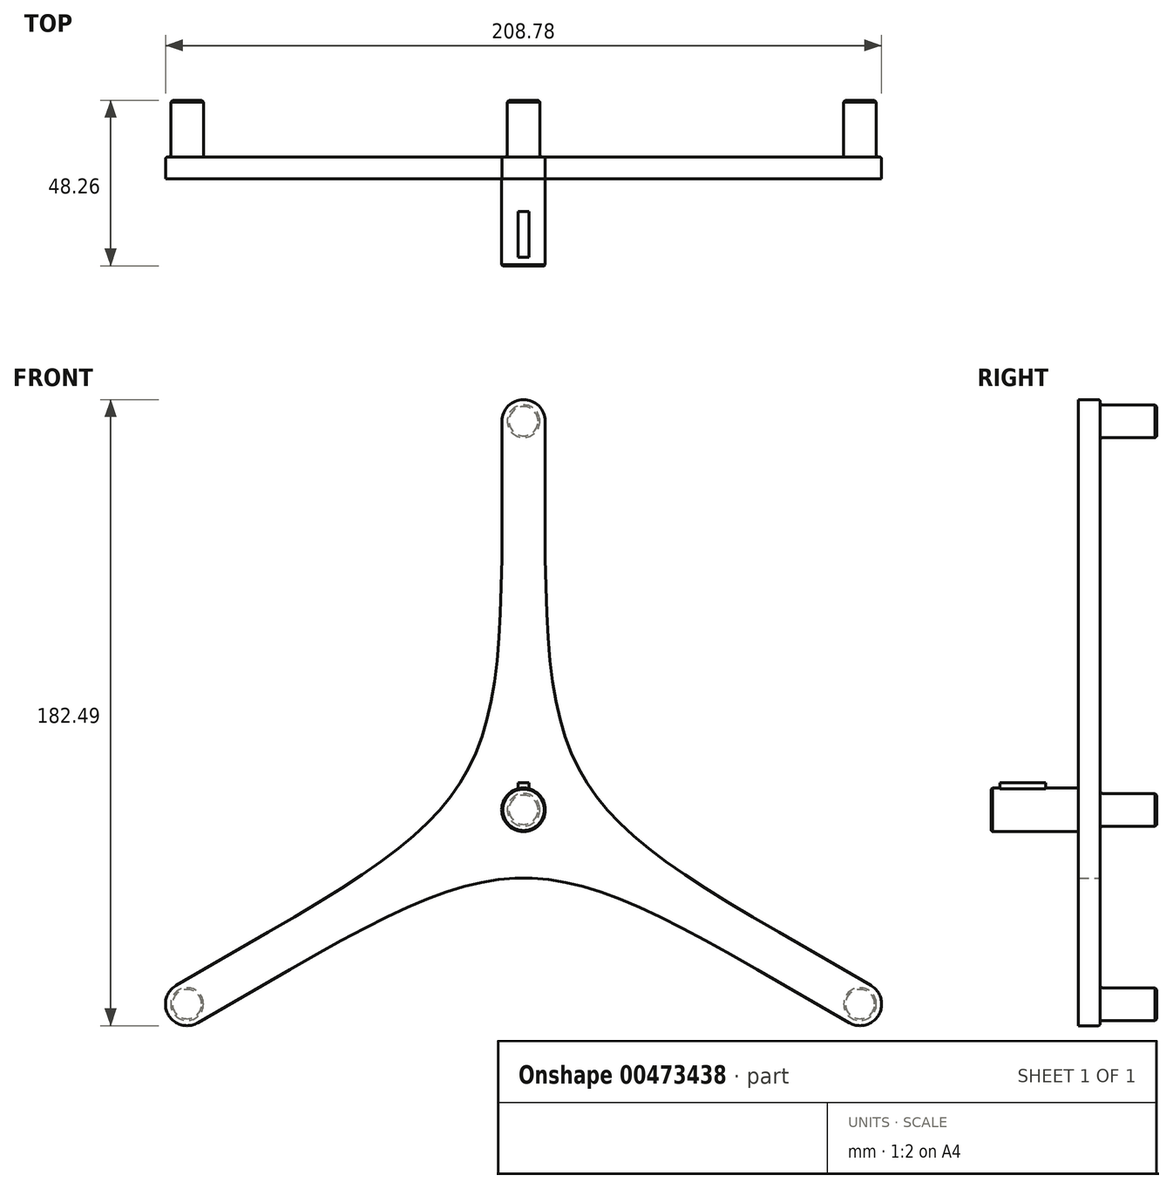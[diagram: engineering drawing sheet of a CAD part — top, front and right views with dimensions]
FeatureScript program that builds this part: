
annotation { "Feature Type Name" : "Feature", "Feature Type Description" : "" }
export const myFeature = defineFeature(function(context is Context, id is Id, definition is map)
    precondition{}
    {
        {
            var Q0;
            Q0=qCreatedBy(makeId("Front.planeOp"),FACE);
            var sketch = newSketch(context, id + "F0", { "sketchPlane" : qUnion([Q0])});
            skArc(sketch, "E0", {"start": v(-6.3, 113.26) * mm, "mid": v(0, 119.56) * mm, "end": v(6.3, 113.26) * mm});
            skArc(sketch, "E1", {"start": v(6.3, 113.26) * mm, "mid": v(0, 113.44) * mm, "end": v(-6.3, 113.26) * mm, "construction": true});
            skCircle(sketch, "E2", {"center": v(0, 113.26) * mm, "radius": 4.76 * mm});
            skLineSegment(sketch, "E3", {"start": v(-6.3, 113.26) * mm, "end": v(-6.3, 11.07) * mm});
            skArc(sketch, "E4.1.0", {"start": v(-94.94, -62.09) * mm, "mid": v(-103.54, -59.78) * mm, "end": v(-101.24, -51.18) * mm});
            skCircle(sketch, "E4.1.2", {"center": v(-98.09, -56.63) * mm, "radius": 4.76 * mm});
            skLineSegment(sketch, "E4.1.3", {"start": v(-94.94, -62.09) * mm, "end": v(-6.43, -10.99) * mm});
            skArc(sketch, "E4.1.5", {"start": v(-101.24, -51.18) * mm, "mid": v(-98.24, -56.72) * mm, "end": v(-94.94, -62.09) * mm, "construction": true});
            skArc(sketch, "E4.2.0", {"start": v(101.24, -51.18) * mm, "mid": v(103.54, -59.78) * mm, "end": v(94.94, -62.09) * mm});
            skCircle(sketch, "E4.2.2", {"center": v(98.09, -56.63) * mm, "radius": 4.76 * mm});
            skLineSegment(sketch, "E4.2.3", {"start": v(101.24, -51.18) * mm, "end": v(12.73, -0.08) * mm});
            skArc(sketch, "E4.2.5", {"start": v(94.94, -62.09) * mm, "mid": v(98.24, -56.72) * mm, "end": v(101.24, -51.18) * mm, "construction": true});
            skLineSegment(sketch, "E5", {"start": v(6.3, 11.07) * mm, "end": v(6.3, 113.26) * mm});
            skCircle(sketch, "E6", {"center": v(0, 0) * mm, "radius": 4.77 * mm});
            skLineSegment(sketch, "E7", {"start": v(6.43, -10.99) * mm, "end": v(94.94, -62.09) * mm});
            skLineSegment(sketch, "E8", {"start": v(-12.73, -0.08) * mm, "end": v(-101.24, -51.18) * mm});
            skLineSegment(sketch, "E9", {"start": v(-6.3, 11.07) * mm, "end": v(-12.73, -0.08) * mm});
            skLineSegment(sketch, "E10", {"start": v(-6.43, -10.99) * mm, "end": v(6.43, -10.99) * mm});
            skLineSegment(sketch, "E11", {"start": v(12.73, -0.08) * mm, "end": v(6.3, 11.07) * mm});
            skFitSpline(sketch, "E12", {"points": [v(6.3, 82.3) * mm, v(74.43, -35.7) * mm], "startDerivative": vector(0, -213.73) * mm, "endDerivative": vector(185.1, -106.86) * mm});
            skFitSpline(sketch, "E13", {"points": [v(-74.43, -35.7) * mm, v(-6.3, 82.3) * mm], "startDerivative": vector(185.1, 106.86) * mm, "endDerivative": vector(0, 213.73) * mm});
            skFitSpline(sketch, "E14", {"points": [v(-68.13, -46.61) * mm, v(68.13, -46.61) * mm], "startDerivative": vector(185.1, 106.86) * mm, "endDerivative": vector(185.1, -106.86) * mm});
            skSolve(sketch);
        }
        {
            var Q0;
            Q0 = qSketchRegion(id + "F0", true);
            var Q1;
            Q1=makeQuery(id+"F0.imprint","IMPRINT",FACE,{"disambiguationData":[TD([[makeQuery(id+"F0.imprint","IMPRINT",EDGE,{"derivedFrom":sQuery(id+"F0.wireOp",EDGE,"E6")}),1.0]])]});
            var Q2;
            Q2=makeQuery(id+"F0.imprint","IMPRINT",FACE,{"disambiguationData":[TD([[makeQuery(id+"F0.imprint","IMPRINT",EDGE,{"derivedFrom":sQuery(id+"F0.wireOp",EDGE,"E2")}),1.0]])]});
            var Q3;
            Q3=makeQuery(id+"F0.imprint","IMPRINT",FACE,{"disambiguationData":[TD([[makeQuery(id+"F0.imprint","IMPRINT",EDGE,{"derivedFrom":sQuery(id+"F0.wireOp",EDGE,"E4.1.2")}),1.0]])]});
            var Q4;
            Q4=makeQuery(id+"F0.imprint","IMPRINT",FACE,{"disambiguationData":[TD([[makeQuery(id+"F0.imprint","IMPRINT",EDGE,{"derivedFrom":sQuery(id+"F0.wireOp",EDGE,"E4.2.2")}),1.0]])]});
            extrude(context, id + "F1", {"entities" : qUnion([Q0, Q1, Q2, Q3, Q4]), "depth" : 6.35 * mm});
        }
        {
            var Q0;
            Q0=makeQuery(id+"F0.imprint","IMPRINT",FACE,{"disambiguationData":[TD([[makeQuery(id+"F0.imprint","IMPRINT",EDGE,{"derivedFrom":sQuery(id+"F0.wireOp",EDGE,"E4.1.2")}),1.0]])]});
            var Q1;
            Q1=makeQuery(id+"F0.imprint","IMPRINT",FACE,{"disambiguationData":[TD([[makeQuery(id+"F0.imprint","IMPRINT",EDGE,{"derivedFrom":sQuery(id+"F0.wireOp",EDGE,"E4.2.2")}),1.0]])]});
            var Q2;
            Q2=makeQuery(id+"F0.imprint","IMPRINT",FACE,{"disambiguationData":[TD([[makeQuery(id+"F0.imprint","IMPRINT",EDGE,{"derivedFrom":sQuery(id+"F0.wireOp",EDGE,"E6")}),1.0]])]});
            var Q3;
            Q3=makeQuery(id+"F0.imprint","IMPRINT",FACE,{"disambiguationData":[TD([[makeQuery(id+"F0.imprint","IMPRINT",EDGE,{"derivedFrom":sQuery(id+"F0.wireOp",EDGE,"E2")}),1.0]])]});
            extrude(context, id + "F2", {"entities" : qUnion([Q0, Q1, Q2, Q3]), "operationType" : NewBodyOperationType.ADD, "oppositeDirection" : true, "depth" : 16.5 * mm});
        }
        {
            var Q0;
            Q0=makeQuery(id+"F2.opExtrude","CAP_EDGE",EDGE,{"disambiguationData":[OSD([sQuery(id+"F0.wireOp",EDGE,"E2")])],"isStart":false});
            var Q1;
            Q1=makeQuery(id+"F2.opExtrude","CAP_EDGE",EDGE,{"disambiguationData":[OSD([sQuery(id+"F0.wireOp",EDGE,"E4.1.2")])],"isStart":false});
            var Q2;
            Q2=makeQuery(id+"F2.opExtrude","CAP_EDGE",EDGE,{"disambiguationData":[OSD([sQuery(id+"F0.wireOp",EDGE,"E4.2.2")])],"isStart":false});
            var Q3;
            Q3=makeQuery(id+"F2.opExtrude","CAP_EDGE",EDGE,{"disambiguationData":[OSD([sQuery(id+"F0.wireOp",EDGE,"E2")])],"isStart":true});
            var Q4;
            Q4=makeQuery(id+"F2.opExtrude","CAP_EDGE",EDGE,{"disambiguationData":[OSD([sQuery(id+"F0.wireOp",EDGE,"E4.1.2")])],"isStart":true});
            var Q5;
            Q5=makeQuery(id+"F2.opExtrude","CAP_EDGE",EDGE,{"disambiguationData":[OSD([sQuery(id+"F0.wireOp",EDGE,"E4.2.2")])],"isStart":true});
            var Q6;
            Q6=makeQuery(id+"F2.opExtrude","CAP_EDGE",EDGE,{"disambiguationData":[OSD([sQuery(id+"F0.wireOp",EDGE,"E6")])],"isStart":false});
            var Q7;
            Q7=makeQuery(id+"F2.opExtrude","CAP_EDGE",EDGE,{"disambiguationData":[OSD([sQuery(id+"F0.wireOp",EDGE,"E6")])],"isStart":true});
            chamfer(context, id + "F3", {"entities" : qUnion([Q0, Q1, Q2, Q3, Q4, Q5, Q6, Q7]), "width" : 0.5 * mm, "tangentPropagation" : true});
        }
        {
            var Q0;
            Q0=makeQuery(id+"F1.opExtrude","CAP_FACE",FACE,{"disambiguationData":[OSD([sQuery(id+"F0.wireOp",EDGE,"E0"),sQuery(id+"F0.wireOp",EDGE,"E3"),sQuery(id+"F0.wireOp",EDGE,"E4.1.0"),sQuery(id+"F0.wireOp",EDGE,"E4.1.3"),sQuery(id+"F0.wireOp",EDGE,"E4.2.0"),sQuery(id+"F0.wireOp",EDGE,"E4.2.3"),sQuery(id+"F0.wireOp",EDGE,"E5"),sQuery(id+"F0.wireOp",EDGE,"E7"),sQuery(id+"F0.wireOp",EDGE,"E8"),sQuery(id+"F0.wireOp",EDGE,"E12"),sQuery(id+"F0.wireOp",EDGE,"E13"),sQuery(id+"F0.wireOp",EDGE,"E14")])],"isStart":true});
            fillet(context, id + "F4", {"entities" : qUnion([Q0]), "radius" : 0.64 * mm, "allowEdgeOverflow" : false});
        }
        {
            var Q0;
            Q0=makeQuery(id+"F1.opExtrude","CAP_FACE",FACE,{"disambiguationData":[OSD([sQuery(id+"F0.wireOp",EDGE,"E0"),sQuery(id+"F0.wireOp",EDGE,"E3"),sQuery(id+"F0.wireOp",EDGE,"E4.1.0"),sQuery(id+"F0.wireOp",EDGE,"E4.1.3"),sQuery(id+"F0.wireOp",EDGE,"E4.2.0"),sQuery(id+"F0.wireOp",EDGE,"E4.2.3"),sQuery(id+"F0.wireOp",EDGE,"E5"),sQuery(id+"F0.wireOp",EDGE,"E7"),sQuery(id+"F0.wireOp",EDGE,"E8"),sQuery(id+"F0.wireOp",EDGE,"E12"),sQuery(id+"F0.wireOp",EDGE,"E13"),sQuery(id+"F0.wireOp",EDGE,"E14")])],"isStart":false});
            var sketch = newSketch(context, id + "F5", { "sketchPlane" : qUnion([Q0])});
            skCircle(sketch, "E15", {"center": v(0, 0) * mm, "radius": 6.35 * mm});
            skLineSegment(sketch, "E16.bottom", {"start": v(-1.59, 4.76) * mm, "end": v(1.59, 4.76) * mm});
            skLineSegment(sketch, "E16.top", {"start": v(-1.59, 7.94) * mm, "end": v(1.59, 7.94) * mm});
            skLineSegment(sketch, "E16.left", {"start": v(-1.59, 4.76) * mm, "end": v(-1.59, 7.94) * mm});
            skLineSegment(sketch, "E16.right", {"start": v(1.59, 4.76) * mm, "end": v(1.59, 7.94) * mm});
            skPoint(sketch, "E16.middle", {"position": v(0, 6.35) * mm});
            skSolve(sketch);
        }
        {
            var Q0;
            {var subQ5=sQuery(id+"F5.wireOp",EDGE,"E16.bottom");Q0=makeQuery(id+"F5.imprint","IMPRINT",FACE,{"disambiguationData":[TD([[makeQuery(id+"F5.imprint","IMPRINT",EDGE,{"derivedFrom":subQ5}),1.0]])]});}
            var Q1;
            {var subQ5=sQuery(id+"F5.wireOp",EDGE,"E16.bottom");Q1=makeQuery(id+"F5.imprint","IMPRINT",FACE,{"disambiguationData":[TD([[makeQuery(id+"F5.imprint","IMPRINT",EDGE,{"derivedFrom":subQ5}),-1.0]])]});}
            extrude(context, id + "F6", {"entities" : qUnion([Q0, Q1]), "operationType" : NewBodyOperationType.ADD, "depth" : 25.4 * mm});
        }
        {
            var Q0;
            {var subQ5=sQuery(id+"F5.wireOp",EDGE,"E16.top");Q0=makeQuery(id+"F5.imprint","IMPRINT",FACE,{"disambiguationData":[TD([[makeQuery(id+"F5.imprint","IMPRINT",EDGE,{"derivedFrom":subQ5}),-1.0]])]});}
            extrude(context, id + "F7", {"entities" : qUnion([Q0]), "operationType" : NewBodyOperationType.ADD, "depth" : 22.86 * mm, "hasSecondDirection" : true, "secondDirectionOppositeDirection" : false, "secondDirectionDepth" : 9.52 * mm});
        }
        {
            var Q0;
            Q0=makeQuery(id+"F6.opExtrude","CAP_EDGE",EDGE,{"disambiguationData":[OSD([sQuery(id+"F5.wireOp",EDGE,"E15")])],"isStart":false});
            chamfer(context, id + "F8", {"entities" : qUnion([Q0]), "width" : 0.32 * mm, "tangentPropagation" : true});
        }
    });
